# Revit family: L4+1_I_2606_OS275
name_source: partatom
category: Porte
units: mm (PartAtom-declared; Revit-internal decimal feet)

## family parameters
Condiviso = No
Host = Muro
Numero OmniClass = 23.30.10.00
Punto di calcolo locali = Sì
Sempre verticale = Sì
Taglio con vuoti quando caricato = Sì
Titolo OmniClass = Doors

## types (4) — shared parameters
Chiusura muro = Per host
Costruzione analitica = <Nessuno>
Descrizione = Libro 4+1 apertura interna
Funzione = Interno
H_Max = 2900 mm
H_Min = 1600 mm
H_maniglia = 1050 mm  [stored 3.44488 ft]
L = 3000 mm  [stored 9.84252 ft]
L1 = 3000 mm  [stored 9.84252 ft]
L_A1 = 618 mm
L_Max = 4000 mm  [stored 13.1234 ft]
L_Min = 1500 mm  [stored 4.92126 ft]
L_vetro = 542 mm
Larghezza = 3000 mm  [stored 9.84252 ft]
Larghezza telaio = 75 mm  [stored 0.246063 ft]
Modello = OS2 75 L
Produttore = Secco Sistemi Spa
Proiezione telaio est. = 25 mm  [stored 0.082021 ft]
Proiezione telaio int. = 25 mm  [stored 0.082021 ft]
URL = https://www.seccosistemi.com
WARNING = Sì
n2_cerniere = 2
n3_cerniere = 3
n4_cerniere = 4
numero_cerniere = 3

## per-type parameters (varying)
| type | Altezza | H | H1 | H_A | H_vetro | MATERIALE |
| Acciaio zincato | 3000 mm  [stored 9.84252 ft] | 2900 mm | 2900 mm | 2869 mm | 2798 mm | Acciaio |
| Acciaio inox | 3000 mm  [stored 9.84252 ft] | 2900 mm | 2900 mm | 2869 mm | 2798 mm | Acciaio inox, spazzolato |
| Ottone | 2600 mm  [stored 8.53018 ft] | 2600 mm  [stored 8.53018 ft] | 2600 mm  [stored 8.53018 ft] | 2569 mm | 2498 mm | Ottone |
| Acciaio Corten | 3000 mm  [stored 9.84252 ft] | 2900 mm | 2900 mm | 2869 mm | 2798 mm | Acciaio corten |

note: [stored X ft] marks values corroborated as IEEE doubles in the binary element streams (Revit-internal decimal feet)
